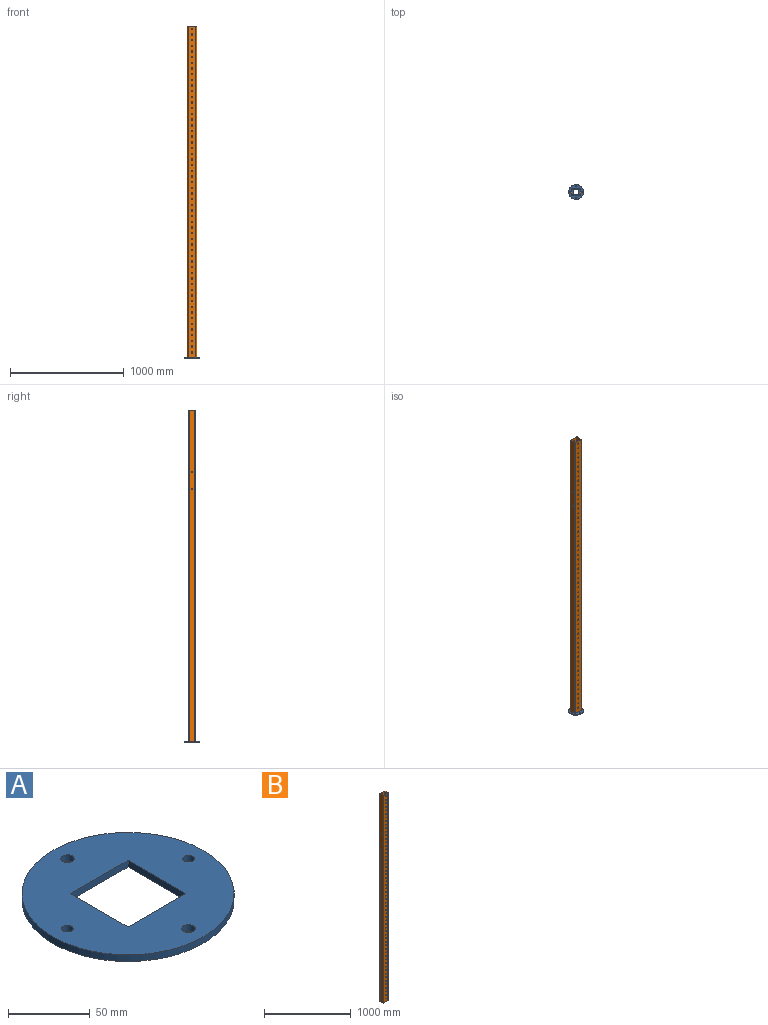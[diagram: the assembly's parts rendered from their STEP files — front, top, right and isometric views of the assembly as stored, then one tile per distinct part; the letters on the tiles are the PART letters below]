
ASSEMBLY  parts=2 mates=1
PART A: 11 faces, bbox 130x130x5 mm
  f0: plane 50x5mm, normal (1,0,0), area 250mm2, adj f1,f7,f9,f10
  f1: plane 50x5mm, normal (0,-1,0), area 250mm2, adj f0,f2,f9,f10
  f2: plane 50x5mm, normal (-1,0,0), area 250mm2, adj f1,f7,f9,f10
  f3: cylinder r=4.1mm len=8.2mm, axis (0,0,-1), area 128.8mm2, adj f9,f10
  f4: cylinder r=4.1mm len=8.2mm, axis (0,0,-1), area 128.8mm2, adj f9,f10
  f5: cylinder r=3.5mm len=7mm, axis (0,0,-1), area 110mm2, adj f9,f10
  f6: cylinder r=3.5mm len=7mm, axis (0,0,-1), area 110mm2, adj f9,f10
  f7: plane 50x5mm, normal (0,1,0), area 250mm2, adj f0,f2,f9,f10
  f8: cylinder r=65mm len=130mm, axis (0,0,-1), area 2042mm2, adj f9,f10
  f9: plane 130x130mm, normal (0,0,1), area 10590.6mm2, adj f0,f1,f2,f3,f4,f5,f6,f7
  f10: plane 130x130mm, normal (0,0,-1), area 10590.6mm2, adj f0,f1,f2,f3,f4,f5,f6,f7
PART B: 138 faces, bbox 80x60x2920 mm
  f0: plane 2920x48mm, normal (1,0,0), area 139926.2mm2, adj f8,f9,f128,f129,f130,f133
  f1: plane 2920x68mm, normal (0,-1,0), area 191779.9mm2, adj f8,f9,f68,f69,f70,f71,f72,f73
  f2: plane 2920x48mm, normal (-1,0,0), area 139926.2mm2, adj f8,f9,f126,f127,f131,f132
  f3: plane 2920x48mm, normal (-1,0,0), area 139926.2mm2, adj f8,f9,f128,f129,f134,f137
  f4: plane 2920x68mm, normal (0,-1,0), area 191779.9mm2, adj f8,f9,f10,f11,f12,f13,f14,f15
  f5: plane 2920x48mm, normal (1,0,0), area 139926.2mm2, adj f8,f9,f126,f127,f135,f136
  f6: plane 2920x68mm, normal (0,1,0), area 191779.9mm2, adj f8,f9,f68,f69,f70,f71,f72,f73
  f7: plane 2920x68mm, normal (0,1,0), area 191779.9mm2, adj f8,f9,f10,f11,f12,f13,f14,f15
  f8: plane 80x60mm, normal (0,0,1), area 1028.5mm2, adj f0,f1,f2,f3,f4,f5,f6,f7
  f9: plane 80x60mm, normal (0,0,-1), area 1028.5mm2, adj f0,f1,f2,f3,f4,f5,f6,f7
  f10: cylinder r=6.1mm len=12.2mm, axis (0,-1,0), area 153.3mm2, adj f4,f7
  f11: cylinder r=6.1mm len=12.2mm, axis (0,-1,0), area 153.3mm2, adj f4,f7
  f12: cylinder r=6.1mm len=12.2mm, axis (0,-1,0), area 153.3mm2, adj f4,f7
  f13: cylinder r=6.1mm len=12.2mm, axis (0,-1,0), area 153.3mm2, adj f4,f7
  f14: cylinder r=6.1mm len=12.2mm, axis (0,-1,0), area 153.3mm2, adj f4,f7
  f15: cylinder r=6.1mm len=12.2mm, axis (0,-1,0), area 153.3mm2, adj f4,f7
  f16: cylinder r=6.1mm len=12.2mm, axis (0,-1,0), area 153.3mm2, adj f4,f7
  f17: cylinder r=6.1mm len=12.2mm, axis (0,-1,0), area 153.3mm2, adj f4,f7
  f18: cylinder r=6.1mm len=12.2mm, axis (0,-1,0), area 153.3mm2, adj f4,f7
  f19: cylinder r=6.1mm len=12.2mm, axis (0,-1,0), area 153.3mm2, adj f4,f7
  f20: cylinder r=6.1mm len=12.2mm, axis (0,-1,0), area 153.3mm2, adj f4,f7
  f21: cylinder r=6.1mm len=12.2mm, axis (0,-1,0), area 153.3mm2, adj f4,f7
  f22: cylinder r=6.1mm len=12.2mm, axis (0,-1,0), area 153.3mm2, adj f4,f7
  f23: cylinder r=6.1mm len=12.2mm, axis (0,-1,0), area 153.3mm2, adj f4,f7
  f24: cylinder r=6.1mm len=12.2mm, axis (0,-1,0), area 153.3mm2, adj f4,f7
  f25: cylinder r=6.1mm len=12.2mm, axis (0,-1,0), area 153.3mm2, adj f4,f7
  f26: cylinder r=6.1mm len=12.2mm, axis (0,-1,0), area 153.3mm2, adj f4,f7
  f27: cylinder r=6.1mm len=12.2mm, axis (0,-1,0), area 153.3mm2, adj f4,f7
  f28: cylinder r=6.1mm len=12.2mm, axis (0,-1,0), area 153.3mm2, adj f4,f7
  f29: cylinder r=6.1mm len=12.2mm, axis (0,-1,0), area 153.3mm2, adj f4,f7
  f30: cylinder r=6.1mm len=12.2mm, axis (0,-1,0), area 153.3mm2, adj f4,f7
  f31: cylinder r=6.1mm len=12.2mm, axis (0,-1,0), area 153.3mm2, adj f4,f7
  f32: cylinder r=6.1mm len=12.2mm, axis (0,-1,0), area 153.3mm2, adj f4,f7
  f33: cylinder r=6.1mm len=12.2mm, axis (0,-1,0), area 153.3mm2, adj f4,f7
  f34: cylinder r=6.1mm len=12.2mm, axis (0,-1,0), area 153.3mm2, adj f4,f7
  f35: cylinder r=6.1mm len=12.2mm, axis (0,-1,0), area 153.3mm2, adj f4,f7
  f36: cylinder r=6.1mm len=12.2mm, axis (0,-1,0), area 153.3mm2, adj f4,f7
  f37: cylinder r=6.1mm len=12.2mm, axis (0,-1,0), area 153.3mm2, adj f4,f7
  f38: cylinder r=6.1mm len=12.2mm, axis (0,-1,0), area 153.3mm2, adj f4,f7
  f39: cylinder r=6.1mm len=12.2mm, axis (0,-1,0), area 153.3mm2, adj f4,f7
  f40: cylinder r=6.1mm len=12.2mm, axis (0,-1,0), area 153.3mm2, adj f4,f7
  f41: cylinder r=6.1mm len=12.2mm, axis (0,-1,0), area 153.3mm2, adj f4,f7
  f42: cylinder r=6.1mm len=12.2mm, axis (0,-1,0), area 153.3mm2, adj f4,f7
  f43: cylinder r=6.1mm len=12.2mm, axis (0,-1,0), area 153.3mm2, adj f4,f7
  f44: cylinder r=6.1mm len=12.2mm, axis (0,-1,0), area 153.3mm2, adj f4,f7
  f45: cylinder r=6.1mm len=12.2mm, axis (0,-1,0), area 153.3mm2, adj f4,f7
  f46: cylinder r=6.1mm len=12.2mm, axis (0,-1,0), area 153.3mm2, adj f4,f7
  f47: cylinder r=6.1mm len=12.2mm, axis (0,-1,0), area 153.3mm2, adj f4,f7
  f48: cylinder r=6.1mm len=12.2mm, axis (0,-1,0), area 153.3mm2, adj f4,f7
  f49: cylinder r=6.1mm len=12.2mm, axis (0,-1,0), area 153.3mm2, adj f4,f7
  f50: cylinder r=6.1mm len=12.2mm, axis (0,-1,0), area 153.3mm2, adj f4,f7
  f51: cylinder r=6.1mm len=12.2mm, axis (0,-1,0), area 153.3mm2, adj f4,f7
  f52: cylinder r=6.1mm len=12.2mm, axis (0,-1,0), area 153.3mm2, adj f4,f7
  f53: cylinder r=6.1mm len=12.2mm, axis (0,-1,0), area 153.3mm2, adj f4,f7
  f54: cylinder r=6.1mm len=12.2mm, axis (0,-1,0), area 153.3mm2, adj f4,f7
  f55: cylinder r=6.1mm len=12.2mm, axis (0,-1,0), area 153.3mm2, adj f4,f7
  f56: cylinder r=6.1mm len=12.2mm, axis (0,-1,0), area 153.3mm2, adj f4,f7
  f57: cylinder r=6.1mm len=12.2mm, axis (0,-1,0), area 153.3mm2, adj f4,f7
  f58: cylinder r=6.1mm len=12.2mm, axis (0,-1,0), area 153.3mm2, adj f4,f7
  f59: cylinder r=6.1mm len=12.2mm, axis (0,-1,0), area 153.3mm2, adj f4,f7
  f60: cylinder r=6.1mm len=12.2mm, axis (0,-1,0), area 153.3mm2, adj f4,f7
  f61: cylinder r=6.1mm len=12.2mm, axis (0,-1,0), area 153.3mm2, adj f4,f7
  f62: cylinder r=6.1mm len=12.2mm, axis (0,-1,0), area 153.3mm2, adj f4,f7
  f63: cylinder r=6.1mm len=12.2mm, axis (0,-1,0), area 153.3mm2, adj f4,f7
  f64: cylinder r=6.1mm len=12.2mm, axis (0,-1,0), area 153.3mm2, adj f4,f7
  f65: cylinder r=6.1mm len=12.2mm, axis (0,-1,0), area 153.3mm2, adj f4,f7
  f66: cylinder r=6.1mm len=12.2mm, axis (0,-1,0), area 153.3mm2, adj f4,f7
  f67: cylinder r=6.1mm len=12.2mm, axis (0,-1,0), area 153.3mm2, adj f4,f7
  f68: cylinder r=6.1mm len=12.2mm, axis (0,-1,0), area 153.3mm2, adj f1,f6
  f69: cylinder r=6.1mm len=12.2mm, axis (0,-1,0), area 153.3mm2, adj f1,f6
  f70: cylinder r=6.1mm len=12.2mm, axis (0,-1,0), area 153.3mm2, adj f1,f6
  f71: cylinder r=6.1mm len=12.2mm, axis (0,-1,0), area 153.3mm2, adj f1,f6
  f72: cylinder r=6.1mm len=12.2mm, axis (0,-1,0), area 153.3mm2, adj f1,f6
  f73: cylinder r=6.1mm len=12.2mm, axis (0,-1,0), area 153.3mm2, adj f1,f6
  f74: cylinder r=6.1mm len=12.2mm, axis (0,-1,0), area 153.3mm2, adj f1,f6
  f75: cylinder r=6.1mm len=12.2mm, axis (0,-1,0), area 153.3mm2, adj f1,f6
  f76: cylinder r=6.1mm len=12.2mm, axis (0,-1,0), area 153.3mm2, adj f1,f6
  f77: cylinder r=6.1mm len=12.2mm, axis (0,-1,0), area 153.3mm2, adj f1,f6
  f78: cylinder r=6.1mm len=12.2mm, axis (0,-1,0), area 153.3mm2, adj f1,f6
  f79: cylinder r=6.1mm len=12.2mm, axis (0,-1,0), area 153.3mm2, adj f1,f6
  f80: cylinder r=6.1mm len=12.2mm, axis (0,-1,0), area 153.3mm2, adj f1,f6
  f81: cylinder r=6.1mm len=12.2mm, axis (0,-1,0), area 153.3mm2, adj f1,f6
  f82: cylinder r=6.1mm len=12.2mm, axis (0,-1,0), area 153.3mm2, adj f1,f6
  f83: cylinder r=6.1mm len=12.2mm, axis (0,-1,0), area 153.3mm2, adj f1,f6
  f84: cylinder r=6.1mm len=12.2mm, axis (0,-1,0), area 153.3mm2, adj f1,f6
  f85: cylinder r=6.1mm len=12.2mm, axis (0,-1,0), area 153.3mm2, adj f1,f6
  f86: cylinder r=6.1mm len=12.2mm, axis (0,-1,0), area 153.3mm2, adj f1,f6
  f87: cylinder r=6.1mm len=12.2mm, axis (0,-1,0), area 153.3mm2, adj f1,f6
  f88: cylinder r=6.1mm len=12.2mm, axis (0,-1,0), area 153.3mm2, adj f1,f6
  f89: cylinder r=6.1mm len=12.2mm, axis (0,-1,0), area 153.3mm2, adj f1,f6
  f90: cylinder r=6.1mm len=12.2mm, axis (0,-1,0), area 153.3mm2, adj f1,f6
  f91: cylinder r=6.1mm len=12.2mm, axis (0,-1,0), area 153.3mm2, adj f1,f6
  f92: cylinder r=6.1mm len=12.2mm, axis (0,-1,0), area 153.3mm2, adj f1,f6
  f93: cylinder r=6.1mm len=12.2mm, axis (0,-1,0), area 153.3mm2, adj f1,f6
  f94: cylinder r=6.1mm len=12.2mm, axis (0,-1,0), area 153.3mm2, adj f1,f6
  f95: cylinder r=6.1mm len=12.2mm, axis (0,-1,0), area 153.3mm2, adj f1,f6
  f96: cylinder r=6.1mm len=12.2mm, axis (0,-1,0), area 153.3mm2, adj f1,f6
  f97: cylinder r=6.1mm len=12.2mm, axis (0,-1,0), area 153.3mm2, adj f1,f6
  f98: cylinder r=6.1mm len=12.2mm, axis (0,-1,0), area 153.3mm2, adj f1,f6
  f99: cylinder r=6.1mm len=12.2mm, axis (0,-1,0), area 153.3mm2, adj f1,f6
  f100: cylinder r=6.1mm len=12.2mm, axis (0,-1,0), area 153.3mm2, adj f1,f6
  f101: cylinder r=6.1mm len=12.2mm, axis (0,-1,0), area 153.3mm2, adj f1,f6
  f102: cylinder r=6.1mm len=12.2mm, axis (0,-1,0), area 153.3mm2, adj f1,f6
  f103: cylinder r=6.1mm len=12.2mm, axis (0,-1,0), area 153.3mm2, adj f1,f6
  f104: cylinder r=6.1mm len=12.2mm, axis (0,-1,0), area 153.3mm2, adj f1,f6
  f105: cylinder r=6.1mm len=12.2mm, axis (0,-1,0), area 153.3mm2, adj f1,f6
  f106: cylinder r=6.1mm len=12.2mm, axis (0,-1,0), area 153.3mm2, adj f1,f6
  f107: cylinder r=6.1mm len=12.2mm, axis (0,-1,0), area 153.3mm2, adj f1,f6
  f108: cylinder r=6.1mm len=12.2mm, axis (0,-1,0), area 153.3mm2, adj f1,f6
  f109: cylinder r=6.1mm len=12.2mm, axis (0,-1,0), area 153.3mm2, adj f1,f6
  f110: cylinder r=6.1mm len=12.2mm, axis (0,-1,0), area 153.3mm2, adj f1,f6
  f111: cylinder r=6.1mm len=12.2mm, axis (0,-1,0), area 153.3mm2, adj f1,f6
  f112: cylinder r=6.1mm len=12.2mm, axis (0,-1,0), area 153.3mm2, adj f1,f6
  f113: cylinder r=6.1mm len=12.2mm, axis (0,-1,0), area 153.3mm2, adj f1,f6
  f114: cylinder r=6.1mm len=12.2mm, axis (0,-1,0), area 153.3mm2, adj f1,f6
  f115: cylinder r=6.1mm len=12.2mm, axis (0,-1,0), area 153.3mm2, adj f1,f6
  f116: cylinder r=6.1mm len=12.2mm, axis (0,-1,0), area 153.3mm2, adj f1,f6
  f117: cylinder r=6.1mm len=12.2mm, axis (0,-1,0), area 153.3mm2, adj f1,f6
  f118: cylinder r=6.1mm len=12.2mm, axis (0,-1,0), area 153.3mm2, adj f1,f6
  f119: cylinder r=6.1mm len=12.2mm, axis (0,-1,0), area 153.3mm2, adj f1,f6
  f120: cylinder r=6.1mm len=12.2mm, axis (0,-1,0), area 153.3mm2, adj f1,f6
  f121: cylinder r=6.1mm len=12.2mm, axis (0,-1,0), area 153.3mm2, adj f1,f6
  f122: cylinder r=6.1mm len=12.2mm, axis (0,-1,0), area 153.3mm2, adj f1,f6
  f123: cylinder r=6.1mm len=12.2mm, axis (0,-1,0), area 153.3mm2, adj f1,f6
  f124: cylinder r=6.1mm len=12.2mm, axis (0,-1,0), area 153.3mm2, adj f1,f6
  f125: cylinder r=6.1mm len=12.2mm, axis (0,-1,0), area 153.3mm2, adj f1,f6
  f126: cylinder r=6.1mm len=12.2mm, axis (1,0,0), area 153.3mm2, adj f2,f5
  f127: cylinder r=6.1mm len=12.2mm, axis (1,0,0), area 153.3mm2, adj f2,f5
  f128: cylinder r=6.1mm len=12.2mm, axis (1,0,0), area 153.3mm2, adj f0,f3
  f129: cylinder r=6.1mm len=12.2mm, axis (1,0,0), area 153.3mm2, adj f0,f3
  f130: cylinder r=2mm len=2920mm, axis (0,0,-1), area 9173.5mm2, adj f0,f1,f8,f9
  f131: cylinder r=2mm len=2920mm, axis (0,0,1), area 9173.5mm2, adj f1,f2,f8,f9
  f132: cylinder r=2mm len=2920mm, axis (0,0,-1), area 9173.5mm2, adj f2,f7,f8,f9
  f133: cylinder r=2mm len=2920mm, axis (0,0,1), area 9173.5mm2, adj f0,f7,f8,f9
  f134: cylinder r=6mm len=2920mm, axis (0,0,1), area 27520.4mm2, adj f3,f4,f8,f9
  f135: cylinder r=6mm len=2920mm, axis (0,0,-1), area 27520.4mm2, adj f4,f5,f8,f9
  f136: cylinder r=6mm len=2920mm, axis (0,0,1), area 27520.4mm2, adj f5,f6,f8,f9
  f137: cylinder r=6mm len=2920mm, axis (0,0,-1), area 27520.4mm2, adj f3,f6,f8,f9
PLACE A rot(axis=(0,0,1),180deg) t=(-1305.02,-232.23,-559.68)mm
PLACE B t=(-1160.93,-60.6,-554.68)mm
MATE fastened A.f8 <-> B.f9  axis (0,0,1) through (-1197.75,-82,-554.68)mm
